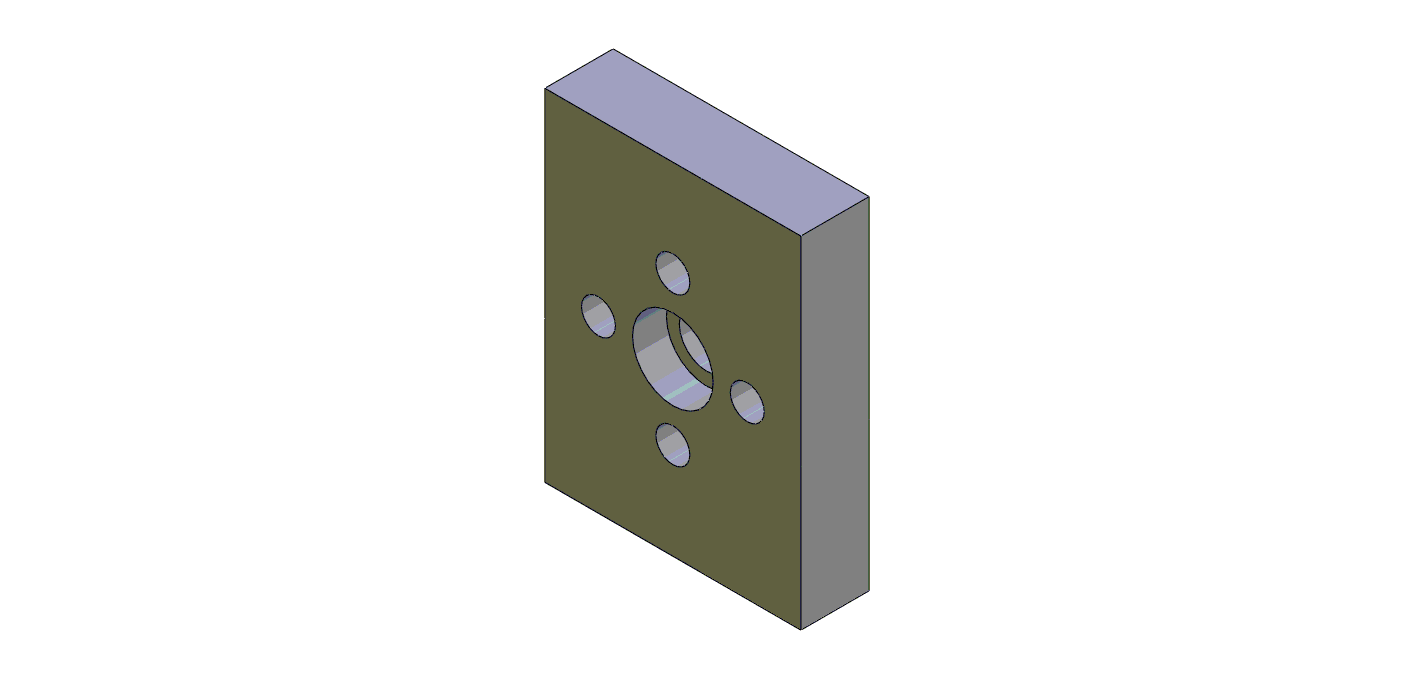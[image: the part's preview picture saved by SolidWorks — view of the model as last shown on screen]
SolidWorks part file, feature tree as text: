
SOLIDWORKS PART (.sldprt)
format: sldprt  version: not decoded by parser v0  size: 149,504 bytes
history: native  units: mm
features: sketch x4, cut_extrude x3, material x1, extrude x1 (+13 scaffold rows collapsed)
feature tree (22):
  scaffold x13  (default folders/planes/origin — collapsed)
  material  "Material <not specified>"
  sketch  "Sketch1"  dims[D1=19.05mm D2=25.4mm]
  extrude  "Boss-Extrude1"  Depth=5.08mm
  sketch  "Sketch2"  dims[D1=5.9944mm]
  cut_extrude  "Cut-Extrude1"  Depth=2.5146mm
  sketch  "Sketch3"  dims[D1=4.064mm]
  cut_extrude  "Cut-Extrude2"  [1 undecoded]
  sketch  "Sketch4"  dims[D1=2.5146mm D2=5.5372mm D3=4.0]
  cut_extrude  "Cut-Extrude4"  [1 undecoded]
decode coverage: 6 of 8 modeling features carry decoded parameters
note: 2 parameter values undecoded
note: suppression state not decoded; provenance and decode notes live in map.json
